# Revit family: 3-640-24B Echo.dwg
name_source: partatom
category: Lighting Fixtures
revit_build: Autodesk Revit 2018 (Build: 20180423_1000(x64)
units: mm (PartAtom-declared; Revit-internal decimal feet)

## family parameters
Always vertical = Yes
Cut with Voids When Loaded = No
Host = Ceiling
Light Source = Yes
OmniClass Number = 23.80.70.11
OmniClass Title = Luminaries for Internal Lighting
Part Type = Normal
Room Calculation Point = No
Round Connector Dimension = Use Diameter
Shared = No

## types (2) — shared parameters
Color Filter = 16777215
Diffusers = Oxygen Lighting - Diffuser - Matte White Acrylic
Dimming Lamp Color Temperature Shift = <None>
Emit Shape Visible in Rendering = No
Emit from Rectangle Length = 30 "
Emit from Rectangle Width = 10 "
Lamp = LED Array
Main Diffuser = Oxygen Lighting - Diffuser - White Opal Glass
Manufacturer = Oxygen Lighting
Model = 3-640-xx / 37-640-xx - Echo
Others = Clear Acrylic
Photometric Web File = 3-640-24 Echo Pendant.ies
Suspension Length = 40 "
Tilt Angle = 90.00°
URL = www.oxygenlighting.com
Wattage Comments = 52.6 W at 120 V
zero-valued in all types: Cost

## per-type parameters (varying)
| type | Metal Finish |
| 3-640-24 / 37-640-24 - Echo | Oxygen Lighting - Metal Finish - 24 - Satin Nickel |
| 3-640-22 / 37-640-22 - Echo | Oxygen Lighting - Metal Finish - 22 - Oiled Bronze |

## geometry (parser evidence)
native form markers: Sweep x11
no freeform markers — native parametric forms only
